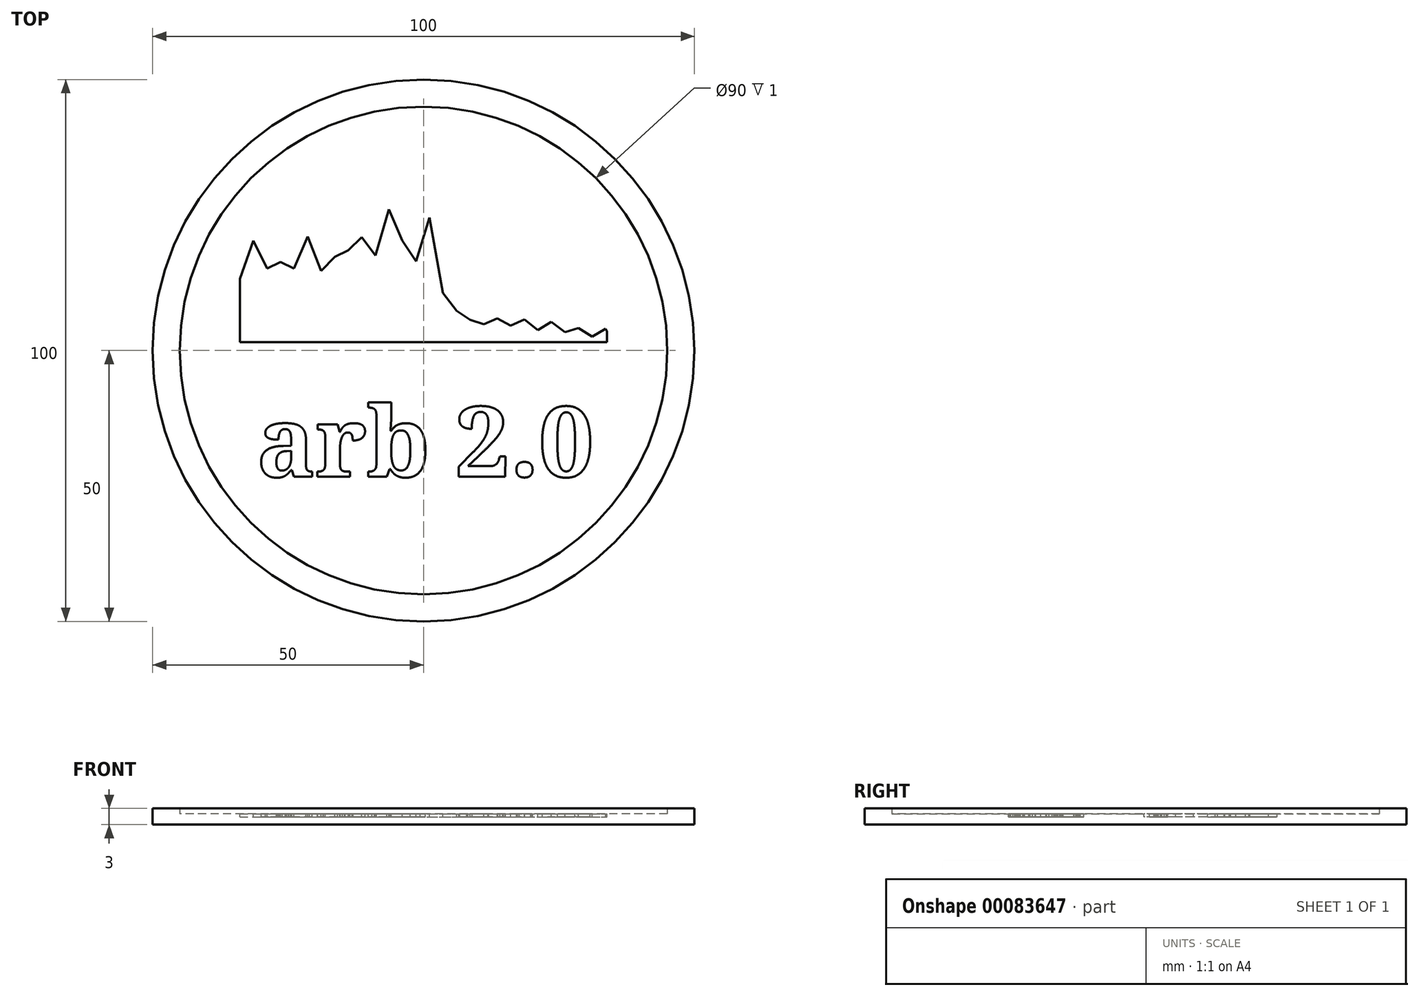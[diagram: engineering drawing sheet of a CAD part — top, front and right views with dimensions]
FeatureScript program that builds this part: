
annotation { "Feature Type Name" : "Feature", "Feature Type Description" : "" }
export const myFeature = defineFeature(function(context is Context, id is Id, definition is map)
    precondition{}
    {
        {
            var Q0;
            Q0=qCreatedBy(makeId("Top.planeOp"),FACE);
            var sketch = newSketch(context, id + "F0", { "sketchPlane" : qUnion([Q0])});
            skCircle(sketch, "E0", {"center": v(0, 0) * mm, "radius": 45 * mm});
            skSolve(sketch);
        }
        {
            var Q0;
            Q0=makeQuery(id+"F0.imprint","IMPRINT",FACE,{"disambiguationData":[TD([[makeQuery(id+"F0.imprint","IMPRINT",EDGE,{"derivedFrom":sQuery(id+"F0.wireOp",EDGE,"E0")}),1.0]])]});
            extrude(context, id + "F1", {"entities" : qUnion([Q0]), "depth" : 2 * mm});
        }
        {
            var Q0;
            Q0=makeQuery(id+"F1.opExtrude","CAP_FACE",FACE,{"disambiguationData":[OSD([sQuery(id+"F0.wireOp",EDGE,"E0")])],"isStart":false});
            var sketch = newSketch(context, id + "F2", { "sketchPlane" : qUnion([Q0])});
            skLineSegment(sketch, "E1.bottom", {"start": v(-33.89, 28.68) * mm, "end": v(33.89, 28.68) * mm});
            skLineSegment(sketch, "E1.top", {"start": v(-33.89, 1.55) * mm, "end": v(33.89, 1.55) * mm});
            skLineSegment(sketch, "E1.left", {"start": v(-33.89, 28.68) * mm, "end": v(-33.89, 1.55) * mm});
            skLineSegment(sketch, "E1.right", {"start": v(33.89, 28.68) * mm, "end": v(33.89, 1.55) * mm});
            skLineSegment(sketch, "E2", {"start": v(-40.09, 20.44) * mm, "end": v(40.09, 20.44) * mm, "construction": true});
            skCircle(sketch, "E3.0", {"center": v(0, 0) * mm, "radius": 50 * mm});
            skLineSegment(sketch, "E4", {"start": v(0, 20.44) * mm, "end": v(0, 45) * mm, "construction": true});
            skLineSegment(sketch, "E5", {"start": v(0, 28.68) * mm, "end": v(0, 20.44) * mm, "construction": true});
            skLineSegment(sketch, "E6", {"start": v(-31.39, 28.68) * mm, "end": v(-31.39, 1.55) * mm, "construction": true});
            skLineSegment(sketch, "E7.1.0.0", {"start": v(-28.89, 28.68) * mm, "end": v(-28.89, 1.55) * mm, "construction": true});
            skLineSegment(sketch, "E7.2.0.0", {"start": v(-26.39, 28.68) * mm, "end": v(-26.39, 1.55) * mm, "construction": true});
            skLineSegment(sketch, "E7.direction1", {"start": v(-31.39, 1.55) * mm, "end": v(-28.89, 1.55) * mm, "construction": true});
            skLineSegment(sketch, "E8.0.3.0", {"start": v(-23.89, 28.68) * mm, "end": v(-23.89, 1.55) * mm, "construction": true});
            skLineSegment(sketch, "E8.0.4.0", {"start": v(-21.39, 28.68) * mm, "end": v(-21.39, 1.55) * mm, "construction": true});
            skLineSegment(sketch, "E8.0.5.0", {"start": v(-18.89, 28.68) * mm, "end": v(-18.89, 1.55) * mm, "construction": true});
            skLineSegment(sketch, "E8.0.6.0", {"start": v(-16.39, 28.68) * mm, "end": v(-16.39, 1.55) * mm, "construction": true});
            skLineSegment(sketch, "E8.0.7.0", {"start": v(-13.89, 28.68) * mm, "end": v(-13.89, 1.55) * mm, "construction": true});
            skLineSegment(sketch, "E8.0.8.0", {"start": v(-11.39, 28.68) * mm, "end": v(-11.39, 1.55) * mm, "construction": true});
            skLineSegment(sketch, "E8.0.9.0", {"start": v(-8.89, 28.68) * mm, "end": v(-8.89, 1.55) * mm, "construction": true});
            skLineSegment(sketch, "E8.0.10.0", {"start": v(-6.39, 28.68) * mm, "end": v(-6.39, 1.55) * mm, "construction": true});
            skLineSegment(sketch, "E8.0.11.0", {"start": v(-3.89, 28.68) * mm, "end": v(-3.89, 1.55) * mm, "construction": true});
            skLineSegment(sketch, "E8.0.12.0", {"start": v(-1.39, 28.68) * mm, "end": v(-1.39, 1.55) * mm, "construction": true});
            skLineSegment(sketch, "E8.0.13.0", {"start": v(1.11, 28.68) * mm, "end": v(1.11, 1.55) * mm, "construction": true});
            skLineSegment(sketch, "E8.0.14.0", {"start": v(3.61, 28.68) * mm, "end": v(3.61, 1.55) * mm, "construction": true});
            skLineSegment(sketch, "E8.0.15.0", {"start": v(6.11, 28.68) * mm, "end": v(6.11, 1.55) * mm, "construction": true});
            skLineSegment(sketch, "E8.0.16.0", {"start": v(8.61, 28.68) * mm, "end": v(8.61, 1.55) * mm, "construction": true});
            skLineSegment(sketch, "E8.0.17.0", {"start": v(11.11, 28.68) * mm, "end": v(11.11, 1.55) * mm, "construction": true});
            skLineSegment(sketch, "E8.0.18.0", {"start": v(13.61, 28.68) * mm, "end": v(13.61, 1.55) * mm, "construction": true});
            skLineSegment(sketch, "E8.0.19.0", {"start": v(16.11, 28.68) * mm, "end": v(16.11, 1.55) * mm, "construction": true});
            skLineSegment(sketch, "E8.0.20.0", {"start": v(18.61, 28.68) * mm, "end": v(18.61, 1.55) * mm, "construction": true});
            skLineSegment(sketch, "E8.0.21.0", {"start": v(21.11, 28.68) * mm, "end": v(21.11, 1.55) * mm, "construction": true});
            skLineSegment(sketch, "E8.0.22.0", {"start": v(23.61, 28.68) * mm, "end": v(23.61, 1.55) * mm, "construction": true});
            skLineSegment(sketch, "E8.0.23.0", {"start": v(26.11, 28.68) * mm, "end": v(26.11, 1.55) * mm, "construction": true});
            skLineSegment(sketch, "E8.0.24.0", {"start": v(28.61, 28.68) * mm, "end": v(28.61, 1.55) * mm, "construction": true});
            skLineSegment(sketch, "E8.0.25.0", {"start": v(31.11, 28.68) * mm, "end": v(31.11, 1.55) * mm, "construction": true});
            skLineSegment(sketch, "E8.0.26.0", {"start": v(33.61, 28.68) * mm, "end": v(33.61, 1.55) * mm, "construction": true});
            skLineSegment(sketch, "E9", {"start": v(-33.89, 13.25) * mm, "end": v(-31.39, 20.28) * mm});
            skLineSegment(sketch, "E10", {"start": v(-31.39, 20.28) * mm, "end": v(-28.89, 15.12) * mm});
            skLineSegment(sketch, "E11", {"start": v(-28.89, 15.12) * mm, "end": v(-26.39, 16.33) * mm});
            skLineSegment(sketch, "E12", {"start": v(-26.39, 16.33) * mm, "end": v(-23.89, 15.12) * mm});
            skLineSegment(sketch, "E13", {"start": v(-23.89, 15.12) * mm, "end": v(-21.39, 21.07) * mm});
            skLineSegment(sketch, "E14", {"start": v(-21.39, 21.07) * mm, "end": v(-18.89, 14.7) * mm});
            skLineSegment(sketch, "E15", {"start": v(-18.89, 14.7) * mm, "end": v(-16.39, 17.3) * mm});
            skLineSegment(sketch, "E16", {"start": v(-16.39, 17.3) * mm, "end": v(-13.89, 18.48) * mm});
            skLineSegment(sketch, "E17", {"start": v(-13.89, 18.48) * mm, "end": v(-11.39, 20.92) * mm});
            skLineSegment(sketch, "E18", {"start": v(-11.39, 20.92) * mm, "end": v(-8.89, 17.56) * mm});
            skLineSegment(sketch, "E19", {"start": v(-8.89, 17.56) * mm, "end": v(-6.39, 26.08) * mm});
            skLineSegment(sketch, "E20", {"start": v(-6.39, 26.08) * mm, "end": v(-3.89, 20.27) * mm});
            skLineSegment(sketch, "E21", {"start": v(-3.89, 20.27) * mm, "end": v(-1.39, 16.45) * mm});
            skLineSegment(sketch, "E22", {"start": v(-1.39, 16.45) * mm, "end": v(1.11, 24.55) * mm});
            skLineSegment(sketch, "E23", {"start": v(1.11, 24.55) * mm, "end": v(3.61, 10.66) * mm});
            skLineSegment(sketch, "E24", {"start": v(3.61, 10.66) * mm, "end": v(6.11, 7.36) * mm});
            skLineSegment(sketch, "E25", {"start": v(6.11, 7.36) * mm, "end": v(8.61, 5.65) * mm});
            skLineSegment(sketch, "E26", {"start": v(8.61, 5.65) * mm, "end": v(11.11, 4.85) * mm});
            skLineSegment(sketch, "E27", {"start": v(11.11, 4.85) * mm, "end": v(13.61, 5.91) * mm});
            skLineSegment(sketch, "E28", {"start": v(13.61, 5.91) * mm, "end": v(16.11, 4.59) * mm});
            skLineSegment(sketch, "E29", {"start": v(16.11, 4.59) * mm, "end": v(18.61, 5.71) * mm});
            skLineSegment(sketch, "E30", {"start": v(18.61, 5.71) * mm, "end": v(21.11, 3.77) * mm});
            skLineSegment(sketch, "E31", {"start": v(21.11, 3.77) * mm, "end": v(23.61, 5.31) * mm});
            skLineSegment(sketch, "E32", {"start": v(23.61, 5.31) * mm, "end": v(26.11, 3.4) * mm});
            skLineSegment(sketch, "E33", {"start": v(26.11, 3.4) * mm, "end": v(28.61, 4.18) * mm});
            skLineSegment(sketch, "E34", {"start": v(28.61, 4.18) * mm, "end": v(31.11, 2.57) * mm});
            skLineSegment(sketch, "E35", {"start": v(31.11, 2.57) * mm, "end": v(33.61, 4.02) * mm});
            skLineSegment(sketch, "E36", {"start": v(33.61, 4.02) * mm, "end": v(33.89, 3.55) * mm});
            skLineSegment(sketch, "E37", {"start": v(-33.89, 6.89) * mm, "end": v(-31.39, 6.89) * mm, "construction": true});
            skSolve(sketch);
        }
        {
            var Q0;
            Q0=qCreatedBy(makeId("Top.planeOp"),FACE);
            var sketch = newSketch(context, id + "F3", { "sketchPlane" : qUnion([Q0])});
            skCircle(sketch, "E38.0", {"center": v(0, 0) * mm, "radius": 50 * mm});
            skCircle(sketch, "E39.0", {"center": v(0, 0) * mm, "radius": 45 * mm});
            skSolve(sketch);
        }
        {
            var Q0;
            Q0 = qSketchRegion(id + "F3", true);
            extrude(context, id + "F4", {"entities" : qUnion([Q0]), "operationType" : NewBodyOperationType.ADD, "depth" : 3 * mm});
        }
        {
            var Q0;
            {var subQ2=sQuery(id+"F2.wireOp",EDGE,"E1.top");Q0=makeQuery(id+"F2.imprint","IMPRINT",FACE,{"disambiguationData":[TD([[makeQuery(id+"F2.imprint","IMPRINT",EDGE,{"derivedFrom":subQ2}),1.0]])]});}
            extrude(context, id + "F5", {"entities" : qUnion([Q0]), "operationType" : NewBodyOperationType.REMOVE, "oppositeDirection" : true, "depth" : 0.6 * mm});
        }
        {
            var Q0;
            Q0=makeQuery(id+"F1.opExtrude","CAP_FACE",FACE,{"disambiguationData":[OSD([sQuery(id+"F0.wireOp",EDGE,"E0")])],"isStart":false});
            var sketch = newSketch(context, id + "F6", { "sketchPlane" : qUnion([Q0])});
            skText(sketch, "E40", { "text": "arb 2.0", "fontName": "NotoSerif-Bold.ttf"});
            skLineSegment(sketch, "E41", {"start": v(-30.77, -9.84) * mm, "end": v(-43.91, -9.84) * mm, "construction": true});
            skLineSegment(sketch, "E42", {"start": v(30.77, -9.84) * mm, "end": v(43.91, -9.84) * mm, "construction": true});
            const initialGuessF6  = {"E40": [-0.03077, -0.0233, 1, 0, 0.013]};
            skSetInitialGuess(sketch, initialGuessF6);
            skSolve(sketch);
        }
        {
            var Q0;
            Q0 = qSketchRegion(id + "F6", true);
            extrude(context, id + "F7", {"entities" : qUnion([Q0]), "operationType" : NewBodyOperationType.REMOVE, "oppositeDirection" : true, "depth" : 0.6 * mm});
        }
    });
